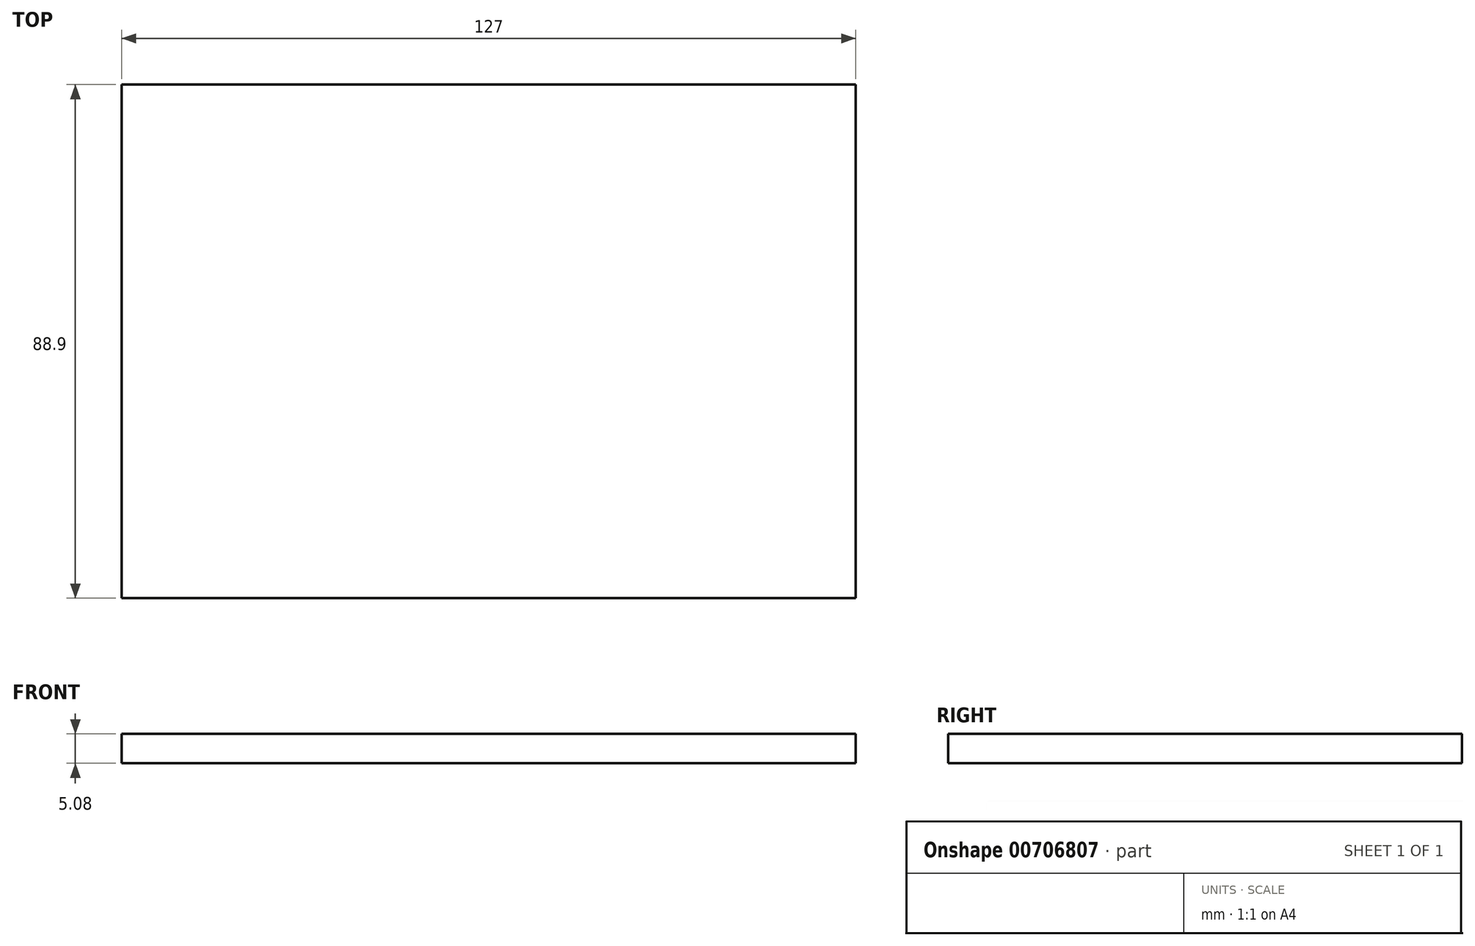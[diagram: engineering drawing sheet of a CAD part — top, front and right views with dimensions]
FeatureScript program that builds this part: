
annotation { "Feature Type Name" : "Feature", "Feature Type Description" : "" }
export const myFeature = defineFeature(function(context is Context, id is Id, definition is map)
    precondition{}
    {
        {
            var Q0;
            Q0=qCreatedBy(makeId("Front.planeOp"),FACE);
            var sketch = newSketch(context, id + "F0", { "sketchPlane" : qUnion([Q0])});
            skLineSegment(sketch, "E0.bottom", {"start": v(-63.5, -2.54) * mm, "end": v(63.5, -2.54) * mm});
            skLineSegment(sketch, "E0.top", {"start": v(-63.5, 2.54) * mm, "end": v(63.5, 2.54) * mm});
            skLineSegment(sketch, "E0.left", {"start": v(-63.5, -2.54) * mm, "end": v(-63.5, 2.54) * mm});
            skLineSegment(sketch, "E0.right", {"start": v(63.5, -2.54) * mm, "end": v(63.5, 2.54) * mm});
            skPoint(sketch, "E0.middle", {"position": v(0, 0) * mm});
            skSolve(sketch);
        }
        {
            var Q0;
            Q0=makeQuery(id+"F0.imprint","IMPRINT",FACE,{"disambiguationData":[TD([[makeQuery(id+"F0.imprint","IMPRINT",EDGE,{"derivedFrom":sQuery(id+"F0.wireOp",EDGE,"E0.bottom")}),1.0]])]});
            extrude(context, id + "F1", {"entities" : qUnion([Q0]), "depth" : 88.9 * mm, "offsetDistance" : 25.4 * mm});
        }
    });
